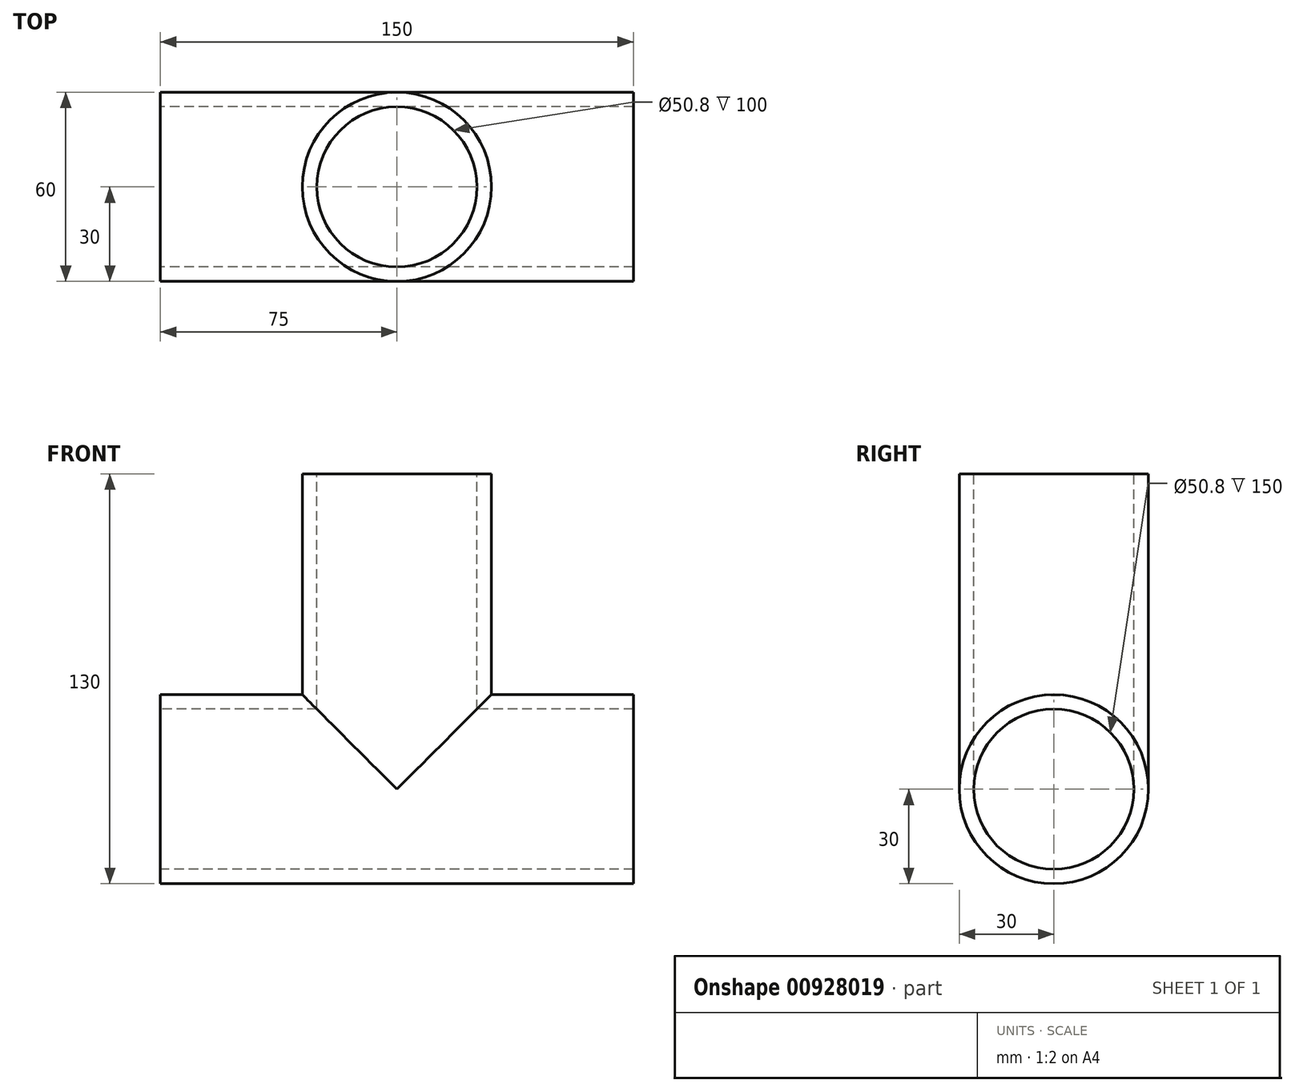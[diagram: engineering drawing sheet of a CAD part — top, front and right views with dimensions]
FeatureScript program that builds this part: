
annotation { "Feature Type Name" : "Feature", "Feature Type Description" : "" }
export const myFeature = defineFeature(function(context is Context, id is Id, definition is map)
    precondition{}
    {
        {
            var Q0;
            Q0=qCreatedBy(makeId("Right.planeOp"),FACE);
            var sketch = newSketch(context, id + "F0", { "sketchPlane" : qUnion([Q0])});
            skCircle(sketch, "E0", {"center": v(0, 0) * mm, "radius": 30 * mm});
            skCircle(sketch, "E1", {"center": v(0, 0) * mm, "radius": 25.4 * mm});
            skSolve(sketch);
        }
        {
            var Q0;
            Q0 = qSketchRegion(id + "F0", true);
            extrude(context, id + "F1", {"entities" : qUnion([Q0]), "endBound" : BoundingType.SYMMETRIC, "depth" : 150 * mm, "offsetDistance" : 25 * mm});
        }
        {
            var Q0;
            Q0=qCreatedBy(makeId("Top.planeOp"),FACE);
            var sketch = newSketch(context, id + "F2", { "sketchPlane" : qUnion([Q0])});
            skCircle(sketch, "E2", {"center": v(0, 0) * mm, "radius": 30 * mm});
            skSolve(sketch);
        }
        {
            var Q0;
            Q0 = qSketchRegion(id + "F2", true);
            extrude(context, id + "F3", {"entities" : qUnion([Q0]), "operationType" : NewBodyOperationType.ADD, "depth" : 100 * mm, "offsetDistance" : 25 * mm});
        }
        {
            var Q0;
            Q0=makeQuery(id+"F3.opExtrude","CAP_FACE",FACE,{"disambiguationData":[OSD([sQuery(id+"F2.wireOp",EDGE,"E2")])],"isStart":false});
            var sketch = newSketch(context, id + "F4", { "sketchPlane" : qUnion([Q0])});
            skCircle(sketch, "E3", {"center": v(0, 0) * mm, "radius": 25.4 * mm});
            skSolve(sketch);
        }
        {
            var Q0;
            Q0 = qSketchRegion(id + "F4", true);
            var Q1;
            Q1=makeQuery(id+"F3.opExtrude","CAP_FACE",FACE,{"disambiguationData":[OSD([sQuery(id+"F2.wireOp",EDGE,"E2")])],"isStart":true});
            extrude(context, id + "F5", {"entities" : qUnion([Q0]), "operationType" : NewBodyOperationType.REMOVE, "endBound" : BoundingType.UP_TO_SURFACE, "oppositeDirection" : true, "depth" : 25 * mm, "endBoundEntityFace" : qUnion([Q1]), "offsetDistance" : 25 * mm});
        }
        {
            var Q0;
            Q0=makeQuery(id+"F1.opExtrude","CAP_FACE",FACE,{"disambiguationData":[OSD([sQuery(id+"F0.wireOp",EDGE,"E0"),sQuery(id+"F0.wireOp",EDGE,"E1")])],"isStart":true});
            var sketch = newSketch(context, id + "F6", { "sketchPlane" : qUnion([Q0])});
            skCircle(sketch, "E4.0", {"center": v(0, 0) * mm, "radius": 25.4 * mm});
            skSolve(sketch);
        }
        {
            var Q0;
            Q0 = qSketchRegion(id + "F6", true);
            var Q1;
            Q1=makeQuery(id+"F1.opExtrude","CAP_FACE",FACE,{"disambiguationData":[OSD([sQuery(id+"F0.wireOp",EDGE,"E0"),sQuery(id+"F0.wireOp",EDGE,"E1")])],"isStart":false});
            extrude(context, id + "F7", {"entities" : qUnion([Q0]), "operationType" : NewBodyOperationType.REMOVE, "endBound" : BoundingType.UP_TO_SURFACE, "oppositeDirection" : true, "depth" : 25 * mm, "endBoundEntityFace" : qUnion([Q1]), "offsetDistance" : 25 * mm});
        }
    });
